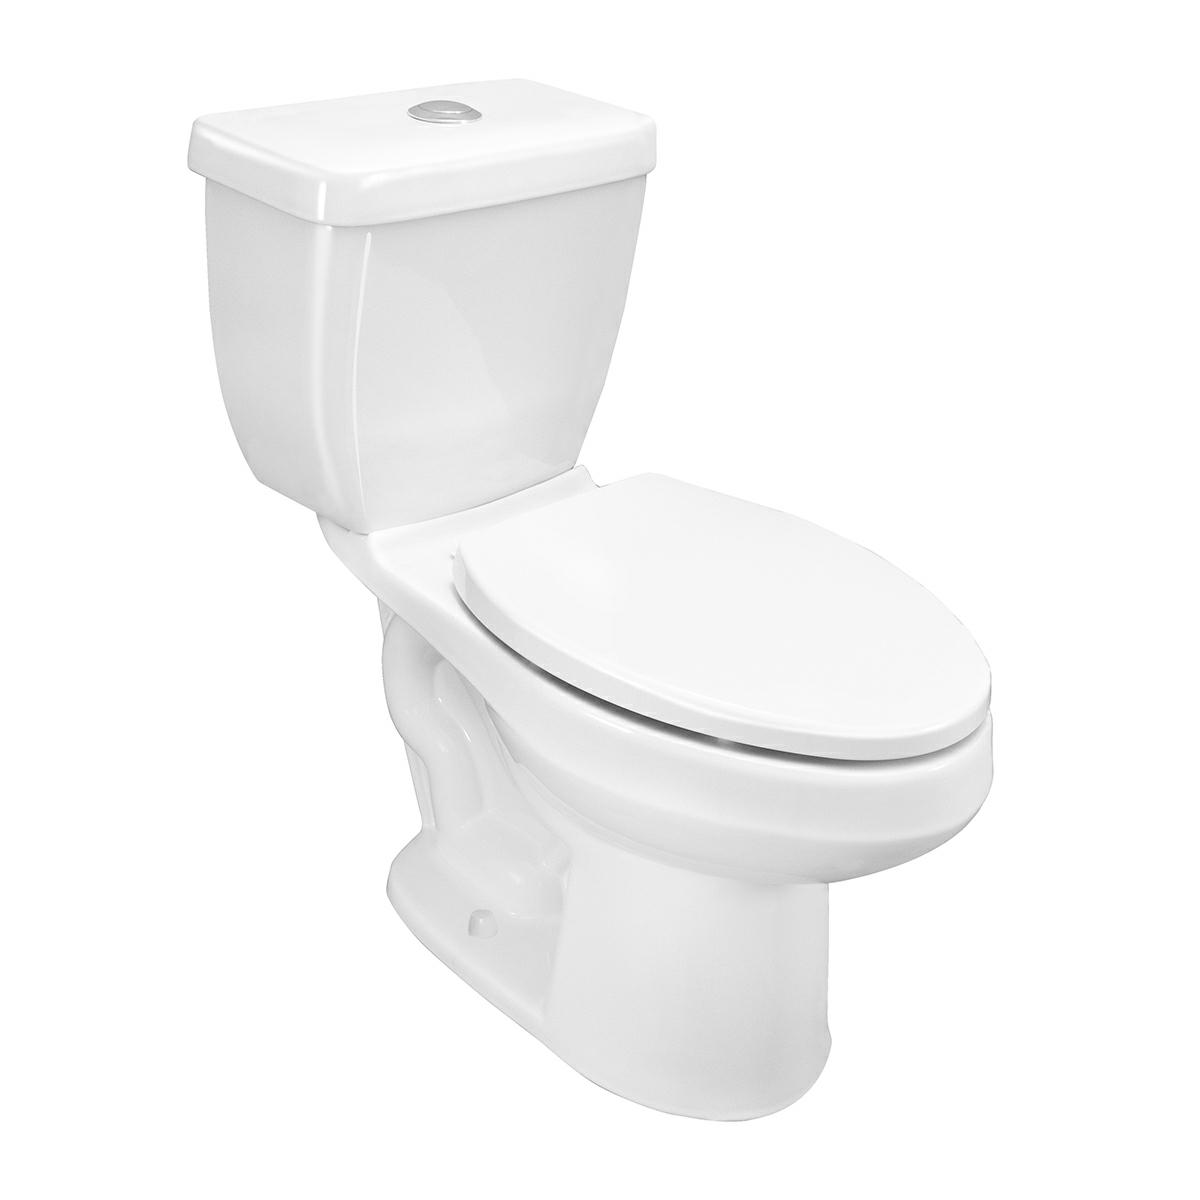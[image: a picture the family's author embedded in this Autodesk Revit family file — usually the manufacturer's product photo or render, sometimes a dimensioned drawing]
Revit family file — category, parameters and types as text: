
# Revit family: WC DRAKAR16_RFA
name_source: partatom
category: Aparatos sanitarios
units: mm (PartAtom-declared; Revit-internal decimal feet)

## family parameters
Compartido = No
Corte con vacíos al cargar = No
Cota de conector redondo = Diámetro de uso
Número OmniClass = 23.45.00.00
Punto de cálculo de habitación = No
Se basa en plano de trabajo = No
Siempre vertical = Sí
Tipo de pieza = Normal
Título OmniClass = Sanitary, Laundry, and Cleaning Equipment

## types (1)
- WC DRAKAR16
    Certification = https://www.helvex.com.mx
    Comentarios de tipo = SANIVEX
    Compliance = NOM-009-CONAGUA-2001
    Conexión AF = Sí
    Data Sheet = https://www.helvex.com.mx
    Descripción = W. C. Taza Tanque Drakar 16", Ecolygico 4,8 l
    Elevación por defecto = 0"
    Fabricante = HELVEX
    Features = Disexo ergonymico de construcciyn robusta
con cerimica de 10mm de espesor, con
sistema de descarga tipo vyrtice con sifyn jet
y espejo de agua yptimo, mueble libre de
alabeo (base plana)
    High Gloss Ceramic = High Gloss Ceramic
    Imagen de tipo = WC DRAKAR16.jpg
    Inlet Threads = Feeding: Ø 15/16" - 14 NS-1 Flush: Coupled With Sanitary Flange
    Max. Working Pressure = 85.3 psi
    Maximum Consumption = 1.26 gpf
    Min. Working Pressure = 14.2 psi
    Modelo = WC DRAKAR16
    Technical Details = Exposed Glazed Trapway; Siphon Action Jetted Bowl; Certified Intake And Flushing Valves; Silent Intake Valve; Flush Valve With Seal; Optimum Water Surface
    Total Height = 31"
    Total Length = 30"
    Total Width = 17"
    URL = https://www.helvex.com.mx
    Warranty = Helvex, S. A. de C. V. garantiza sus productos
cerimicos como libres de defectos en
materiales y procesos de fabricaciyn por 30
axos. En los herrajes por defectos de
manufactura por 5 axos. En el dispositivo TDS
en el mingitorio seco por 3 axos. Tapa y
asiento por un periodo de 2 axos. La vigencia
de la garantta inicia a partir de la fecha de
entrega del producto al consumidor indicada
en esta Pyliza de Garantta.

## geometry (parser evidence)
native form markers: Sweep x3
no freeform markers — native parametric forms only
